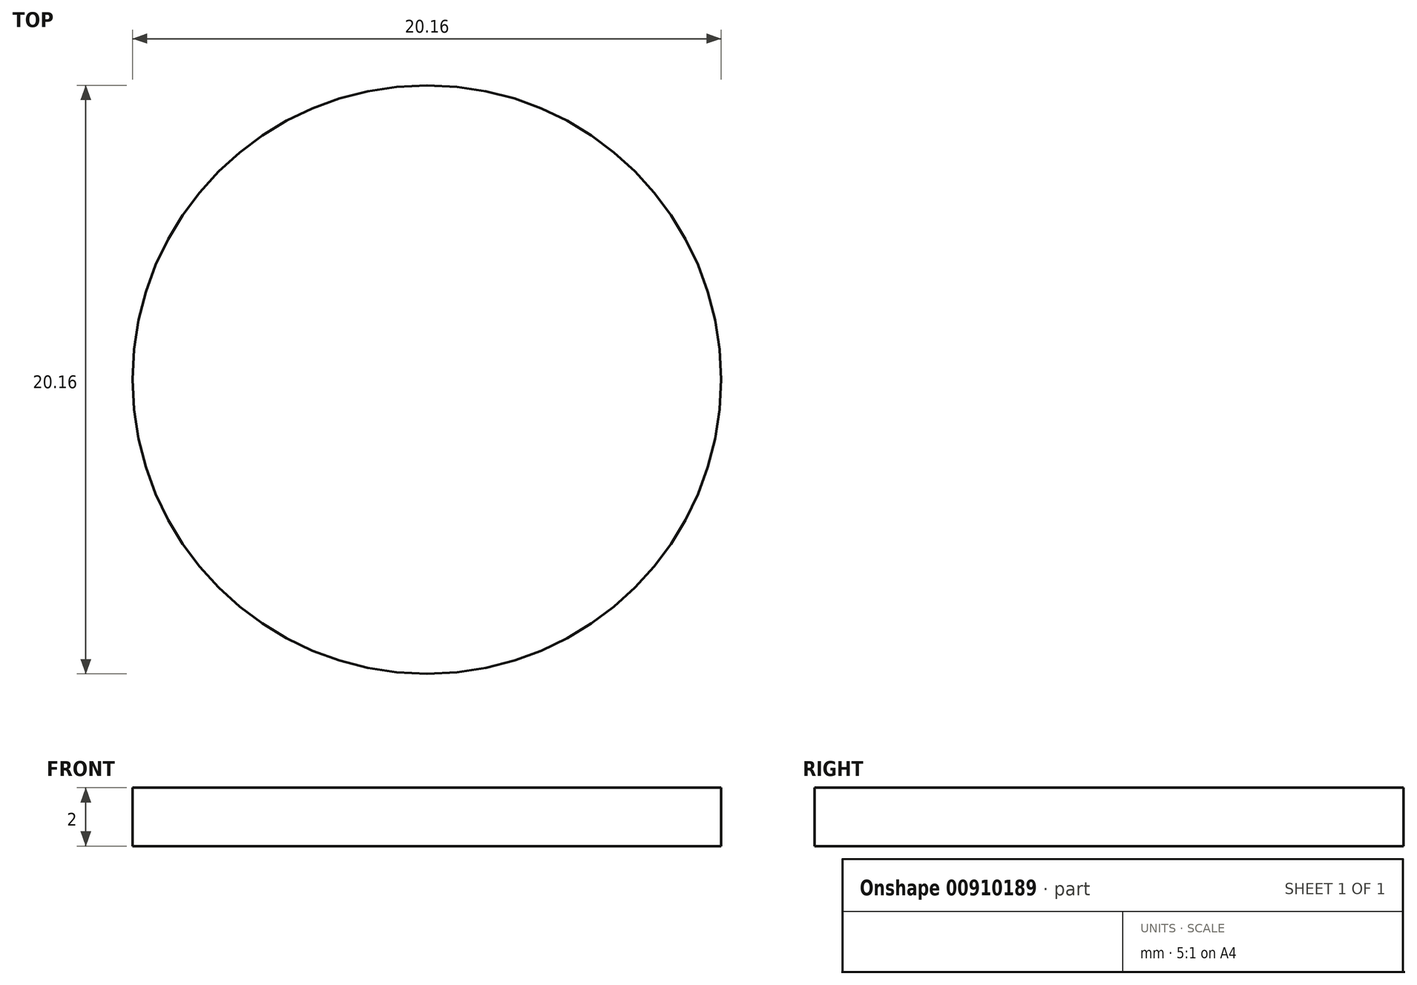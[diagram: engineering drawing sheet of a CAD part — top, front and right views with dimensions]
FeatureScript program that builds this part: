
annotation { "Feature Type Name" : "Feature", "Feature Type Description" : "" }
export const myFeature = defineFeature(function(context is Context, id is Id, definition is map)
    precondition{}
    {
        {
            var Q0;
            Q0=qCreatedBy(makeId("Top.planeOp"),FACE);
            var sketch = newSketch(context, id + "F0", { "sketchPlane" : qUnion([Q0])});
            skCircle(sketch, "E0", {"center": v(0, 0) * mm, "radius": 10.08 * mm});
            skSolve(sketch);
        }
        {
            assignVariable(context, id + "F1", {"name" : "fun", "anyValue" : 2});
        }
        {
            var Q0;
            Q0=makeQuery(id+"F0.imprint","IMPRINT",FACE,{"disambiguationData":[TD([[makeQuery(id+"F0.imprint","IMPRINT",EDGE,{"derivedFrom":sQuery(id+"F0.wireOp",EDGE,"E0")}),1.0]])]});
            extrude(context, id + "F2", {"entities" : qUnion([Q0]), "depth" : (getVariable(context, 'fun')) * mm, "offsetDistance" : 25.4 * mm});
        }
    });
